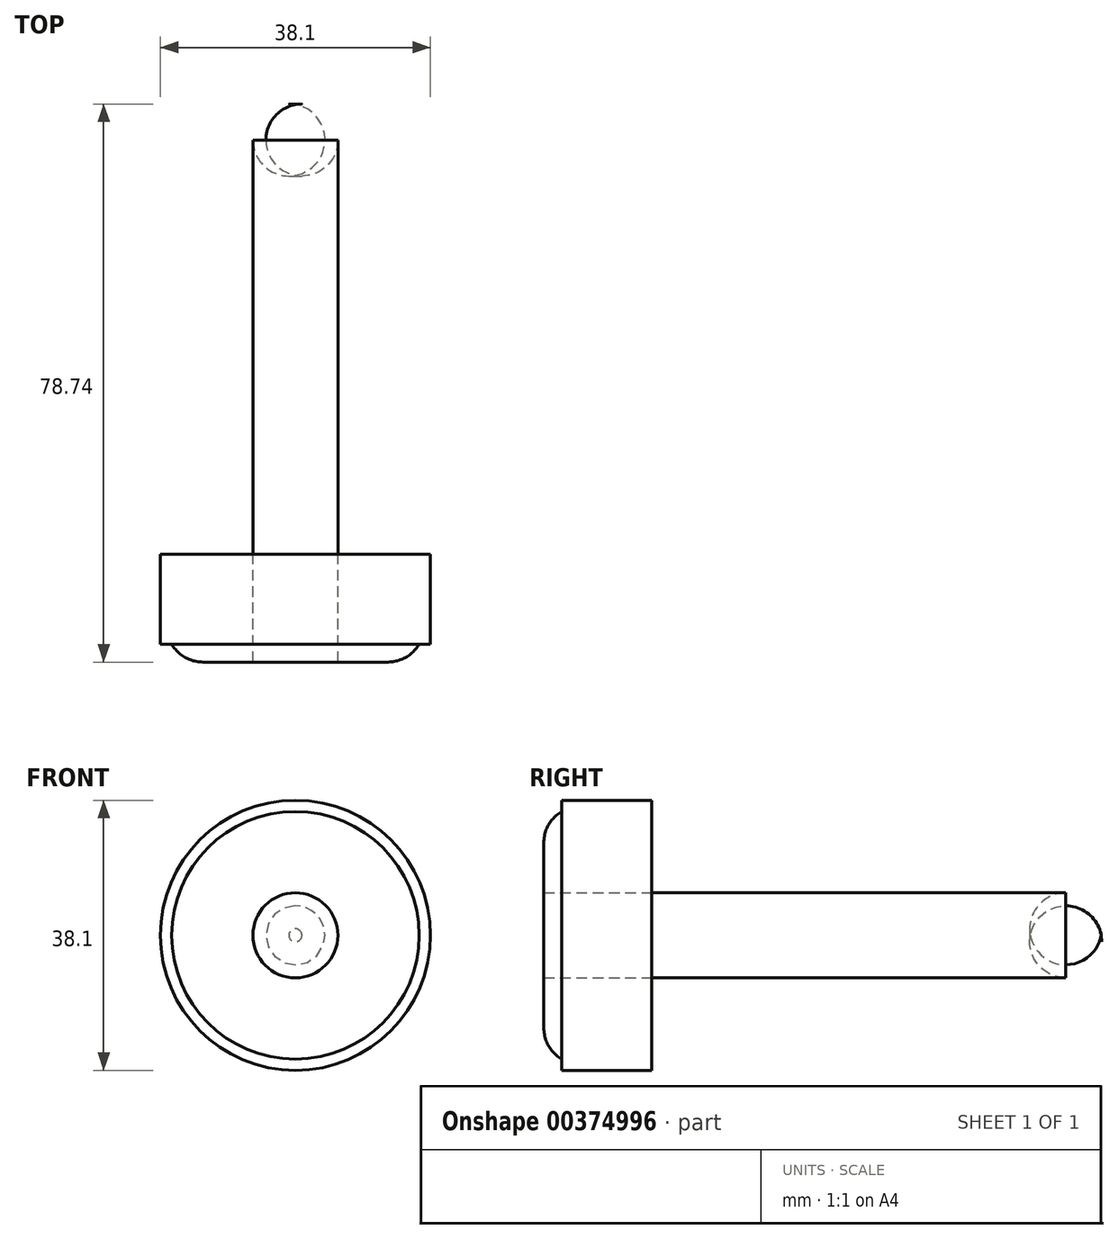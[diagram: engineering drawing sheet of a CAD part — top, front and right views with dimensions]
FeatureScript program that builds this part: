
annotation { "Feature Type Name" : "Feature", "Feature Type Description" : "" }
export const myFeature = defineFeature(function(context is Context, id is Id, definition is map)
    precondition{}
    {
        {
            var Q0;
            Q0=qCreatedBy(makeId("Front.planeOp"),FACE);
            var sketch = newSketch(context, id + "F0", { "sketchPlane" : qUnion([Q0])});
            skCircle(sketch, "E0", {"center": v(0, 0) * mm, "radius": 6 * mm});
            skSolve(sketch);
        }
        {
            var Q0;
            Q0=makeQuery(id+"F0.imprint","IMPRINT",FACE,{"disambiguationData":[TD([[makeQuery(id+"F0.imprint","IMPRINT",EDGE,{"derivedFrom":sQuery(id+"F0.wireOp",EDGE,"E0")}),1.0]])]});
            extrude(context, id + "F1", {"entities" : qUnion([Q0]), "depth" : 63.5 * mm});
        }
        {
            var Q0;
            Q0=makeQuery(id+"F1.opExtrude","CAP_FACE",FACE,{"disambiguationData":[OSD([sQuery(id+"F0.wireOp",EDGE,"E0")])],"isStart":false});
            var sketch = newSketch(context, id + "F2", { "sketchPlane" : qUnion([Q0])});
            skCircle(sketch, "E1", {"center": v(0, 0) * mm, "radius": 19.05 * mm});
            skSolve(sketch);
        }
        {
            var Q0;
            Q0=makeQuery(id+"F2.imprint","IMPRINT",FACE,{"disambiguationData":[TD([[makeQuery(id+"F2.imprint","IMPRINT",EDGE,{"derivedFrom":sQuery(id+"F2.wireOp",EDGE,"E1")}),1.0]])]});
            extrude(context, id + "F3", {"entities" : qUnion([Q0]), "operationType" : NewBodyOperationType.ADD, "depth" : 12.7 * mm});
        }
        {
            var Q0;
            Q0=makeQuery(id+"F3.opExtrude","CAP_FACE",FACE,{"disambiguationData":[OSD([sQuery(id+"F2.wireOp",EDGE,"E1")])],"isStart":false});
            var sketch = newSketch(context, id + "F4", { "sketchPlane" : qUnion([Q0])});
            skCircle(sketch, "E2", {"center": v(0, 0) * mm, "radius": 17.46 * mm});
            skSolve(sketch);
        }
        {
            var Q0;
            Q0=makeQuery(id+"F4.imprint","IMPRINT",FACE,{"disambiguationData":[TD([[makeQuery(id+"F4.imprint","IMPRINT",EDGE,{"derivedFrom":sQuery(id+"F4.wireOp",EDGE,"E2")}),1.0]])]});
            extrude(context, id + "F5", {"entities" : qUnion([Q0]), "operationType" : NewBodyOperationType.ADD, "depth" : 2.54 * mm});
        }
        {
            var Q0;
            Q0=makeQuery(id+"F1.opExtrude","CAP_FACE",FACE,{"disambiguationData":[OSD([sQuery(id+"F0.wireOp",EDGE,"E0")])],"isStart":true});
            fillet(context, id + "F6", {"entities" : qUnion([Q0]), "radius" : 5.08 * mm, "tangentPropagation" : true, "allowEdgeOverflow" : false});
        }
        {
            var Q0;
            Q0=makeQuery(id+"F5.opExtrude","CAP_EDGE",EDGE,{"disambiguationData":[OSD([sQuery(id+"F4.wireOp",EDGE,"E2")])],"isStart":false});
            fillet(context, id + "F7", {"entities" : qUnion([Q0]), "radius" : 5.08 * mm, "tangentPropagation" : true, "allowEdgeOverflow" : false});
        }
    });
